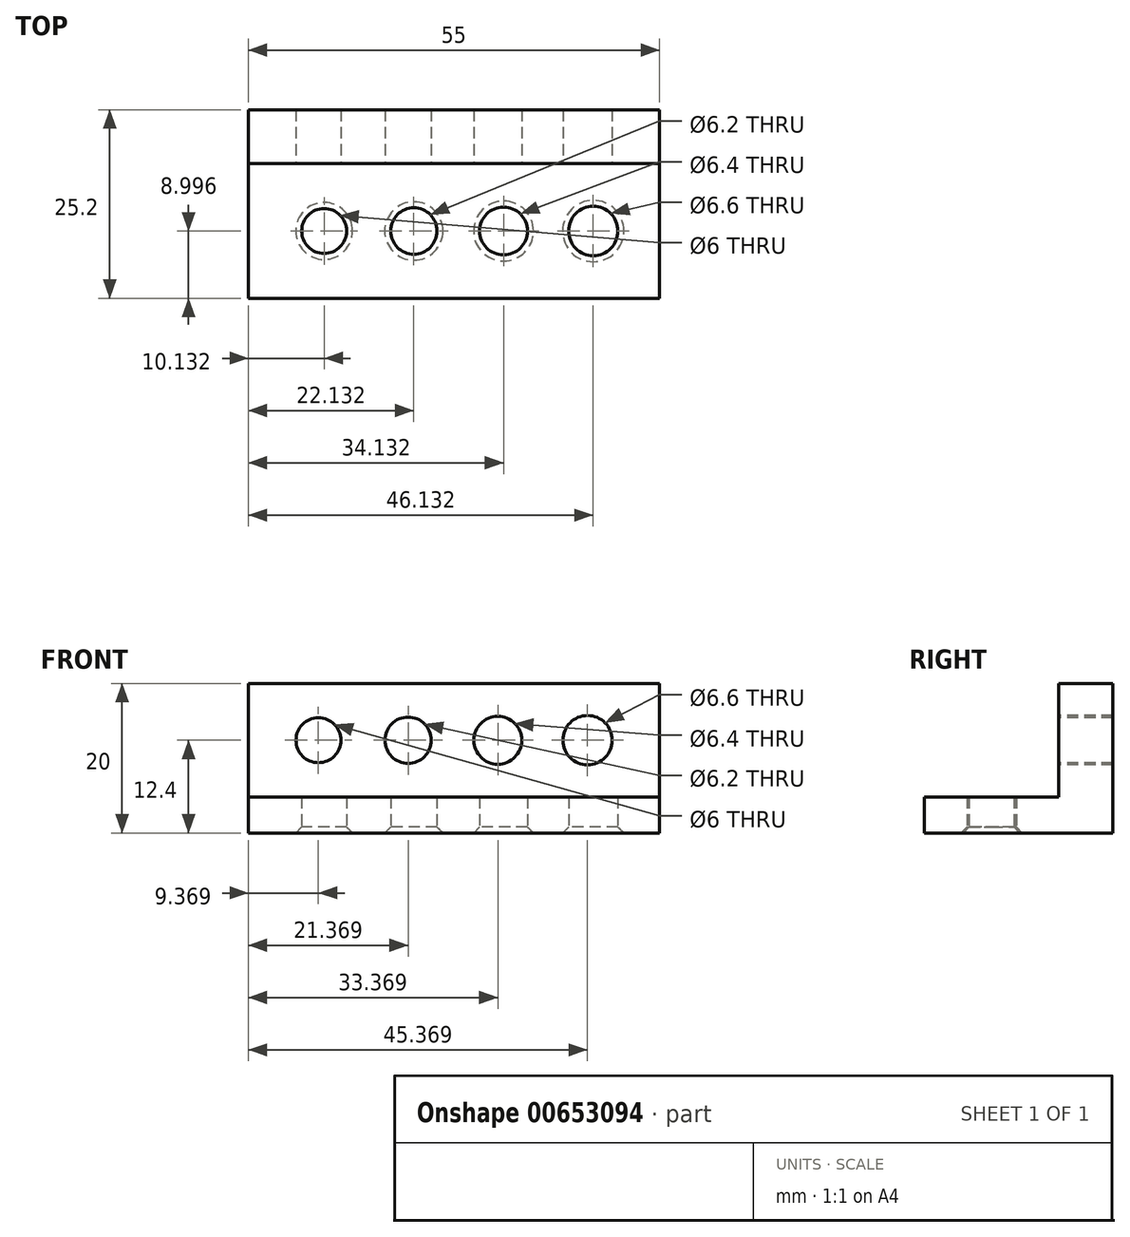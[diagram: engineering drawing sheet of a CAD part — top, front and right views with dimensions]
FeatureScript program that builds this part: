
annotation { "Feature Type Name" : "Feature", "Feature Type Description" : "" }
export const myFeature = defineFeature(function(context is Context, id is Id, definition is map)
    precondition{}
    {
        {
            var Q0;
            Q0=qCreatedBy(makeId("Top.planeOp"),FACE);
            var sketch = newSketch(context, id + "F0", { "sketchPlane" : qUnion([Q0])});
            skCircle(sketch, "E0", {"center": v(-44.87, -8) * mm, "radius": 3 * mm});
            skCircle(sketch, "E1", {"center": v(-32.87, -8) * mm, "radius": 3.1 * mm});
            skCircle(sketch, "E2", {"center": v(-20.87, -8) * mm, "radius": 3.2 * mm});
            skCircle(sketch, "E3", {"center": v(-8.87, -8) * mm, "radius": 3.3 * mm});
            skLineSegment(sketch, "E4.bottom", {"start": v(-55, 1) * mm, "end": v(0, 1) * mm});
            skLineSegment(sketch, "E4.top", {"start": v(-55, -17) * mm, "end": v(0, -17) * mm});
            skLineSegment(sketch, "E4.left", {"start": v(-55, 1) * mm, "end": v(-55, -17) * mm});
            skLineSegment(sketch, "E4.right", {"start": v(0, 1) * mm, "end": v(0, -17) * mm});
            skPoint(sketch, "E5", {"position": v(0, -8) * mm});
            skLineSegment(sketch, "E6.top", {"start": v(-55, 8.2) * mm, "end": v(0, 8.2) * mm});
            skLineSegment(sketch, "E6.left", {"start": v(-55, 1) * mm, "end": v(-55, 8.2) * mm});
            skLineSegment(sketch, "E6.right", {"start": v(0, 1) * mm, "end": v(0, 8.2) * mm});
            skSolve(sketch);
        }
        {
            var Q0;
            Q0=makeQuery(id+"F0.imprint","IMPRINT",FACE,{"disambiguationData":[TD([[makeQuery(id+"F0.imprint","IMPRINT",EDGE,{"derivedFrom":sQuery(id+"F0.wireOp",EDGE,"E0")}),-1.0]])]});
            extrude(context, id + "F1", {"entities" : qUnion([Q0]), "depth" : 4.8 * mm, "offsetDistance" : 25 * mm});
        }
        {
            var Q0;
            Q0=makeQuery(id+"F0.imprint","IMPRINT",FACE,{"disambiguationData":[TD([[makeQuery(id+"F0.imprint","IMPRINT",EDGE,{"derivedFrom":sQuery(id+"F0.wireOp",EDGE,"E4.bottom")}),1.0]])]});
            extrude(context, id + "F2", {"entities" : qUnion([Q0]), "operationType" : NewBodyOperationType.ADD, "depth" : 20 * mm, "offsetDistance" : 25 * mm});
        }
        {
            var Q0;
            Q0=makeQuery(id+"F2.opExtrude","SWEPT_FACE",FACE,{"disambiguationData":[OSD([sQuery(id+"F0.wireOp",EDGE,"E4.bottom")])]});
            var sketch = newSketch(context, id + "F3", { "sketchPlane" : qUnion([Q0])});
            skCircle(sketch, "E7", {"center": v(-45.63, 12.4) * mm, "radius": 3 * mm});
            skCircle(sketch, "E8", {"center": v(-33.63, 12.4) * mm, "radius": 3.1 * mm});
            skCircle(sketch, "E9", {"center": v(-21.63, 12.4) * mm, "radius": 3.2 * mm});
            skCircle(sketch, "E10", {"center": v(-9.63, 12.4) * mm, "radius": 3.3 * mm});
            skPoint(sketch, "E11", {"position": v(0, 12.4) * mm});
            skSolve(sketch);
        }
        {
            var Q0;
            Q0 = qSketchRegion(id + "F3", true);
            extrude(context, id + "F4", {"entities" : qUnion([Q0]), "operationType" : NewBodyOperationType.REMOVE, "oppositeDirection" : true, "depth" : 25 * mm, "offsetDistance" : 25 * mm});
        }
        {
            var Q0;
            Q0=makeQuery(id+"F1.opExtrude","CAP_EDGE",EDGE,{"disambiguationData":[OSD([sQuery(id+"F0.wireOp",EDGE,"E0")])],"isStart":true});
            var Q1;
            Q1=makeQuery(id+"F1.opExtrude","CAP_EDGE",EDGE,{"disambiguationData":[OSD([sQuery(id+"F0.wireOp",EDGE,"E1")])],"isStart":true});
            var Q2;
            Q2=makeQuery(id+"F1.opExtrude","CAP_EDGE",EDGE,{"disambiguationData":[OSD([sQuery(id+"F0.wireOp",EDGE,"E2")])],"isStart":true});
            var Q3;
            Q3=makeQuery(id+"F1.opExtrude","CAP_EDGE",EDGE,{"disambiguationData":[OSD([sQuery(id+"F0.wireOp",EDGE,"E3")])],"isStart":true});
            chamfer(context, id + "F5", {"entities" : qUnion([Q0, Q1, Q2, Q3]), "width" : 0.8 * mm, "tangentPropagation" : true});
        }
    });
